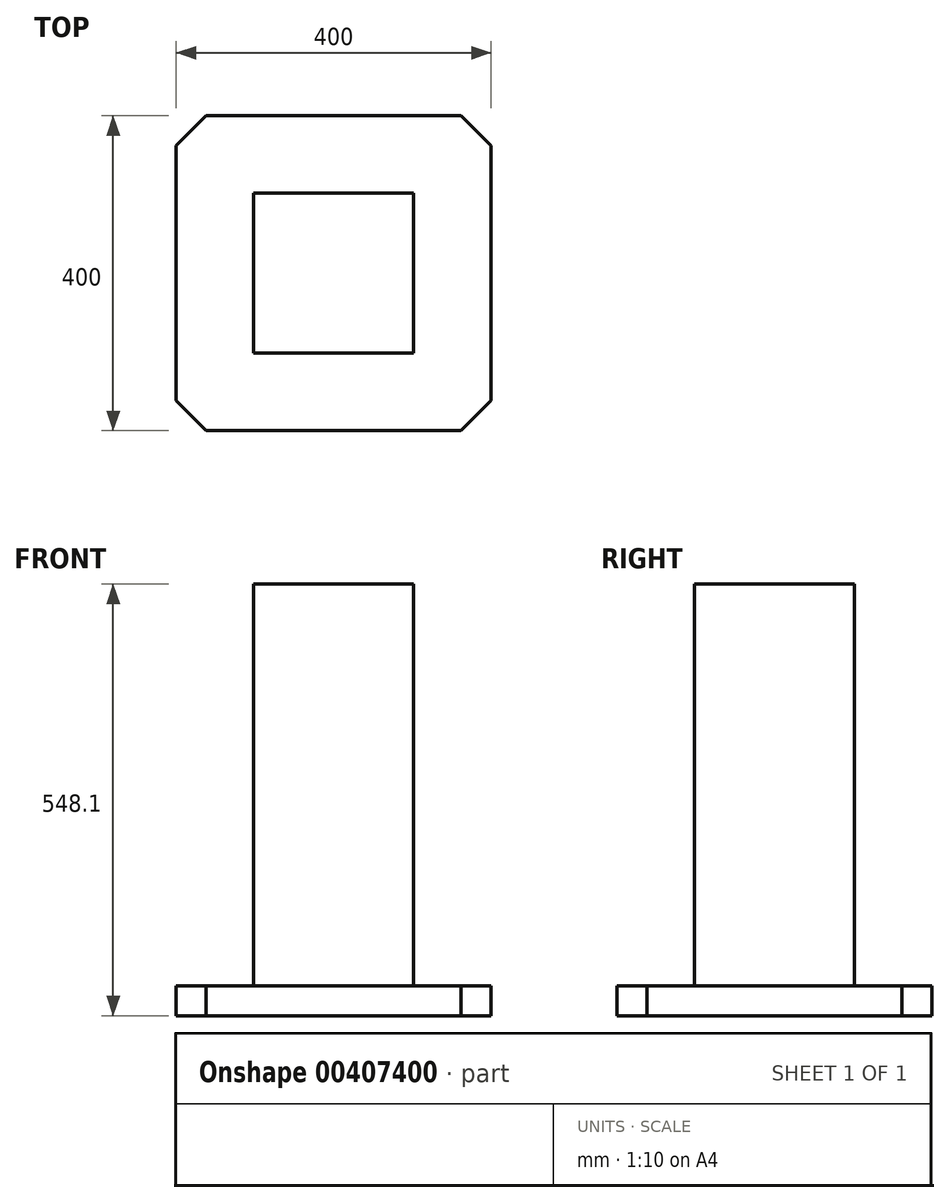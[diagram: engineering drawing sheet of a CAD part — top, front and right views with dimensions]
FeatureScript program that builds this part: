
annotation { "Feature Type Name" : "Feature", "Feature Type Description" : "" }
export const myFeature = defineFeature(function(context is Context, id is Id, definition is map)
    precondition{}
    {
        {
            var Q0;
            Q0=qCreatedBy(makeId("Top.planeOp"),FACE);
            var sketch = newSketch(context, id + "F0", { "sketchPlane" : qUnion([Q0])});
            skLineSegment(sketch, "E0.bottom", {"start": v(200, -200) * mm, "end": v(-200, -200) * mm});
            skLineSegment(sketch, "E0.top", {"start": v(200, 200) * mm, "end": v(-200, 200) * mm});
            skLineSegment(sketch, "E0.left", {"start": v(200, -200) * mm, "end": v(200, 200) * mm});
            skLineSegment(sketch, "E0.right", {"start": v(-200, -200) * mm, "end": v(-200, 200) * mm});
            skPoint(sketch, "E0.middle", {"position": v(0, 0) * mm});
            skSolve(sketch);
        }
        {
            var Q0;
            Q0=makeQuery(id+"F0.imprint","IMPRINT",FACE,{"disambiguationData":[TD([[makeQuery(id+"F0.imprint","IMPRINT",EDGE,{"derivedFrom":sQuery(id+"F0.wireOp",EDGE,"E0.bottom")}),-1.0]])]});
            extrude(context, id + "F1", {"entities" : qUnion([Q0]), "depth" : 38.1 * mm});
        }
        {
            var Q0;
            Q0=makeQuery(id+"F1.opExtrude","SWEPT_EDGE",EDGE,{"disambiguationData":[OSD([sQuery(id+"F0.wireOp",EDGE,"E0.top"),sQuery(id+"F0.wireOp",EDGE,"E0.right")])]});
            var Q1;
            Q1=makeQuery(id+"F1.opExtrude","SWEPT_EDGE",EDGE,{"disambiguationData":[OSD([sQuery(id+"F0.wireOp",EDGE,"E0.bottom"),sQuery(id+"F0.wireOp",EDGE,"E0.right")])]});
            var Q2;
            Q2=makeQuery(id+"F1.opExtrude","SWEPT_EDGE",EDGE,{"disambiguationData":[OSD([sQuery(id+"F0.wireOp",EDGE,"E0.bottom"),sQuery(id+"F0.wireOp",EDGE,"E0.left")])]});
            var Q3;
            Q3=makeQuery(id+"F1.opExtrude","SWEPT_EDGE",EDGE,{"disambiguationData":[OSD([sQuery(id+"F0.wireOp",EDGE,"E0.top"),sQuery(id+"F0.wireOp",EDGE,"E0.left")])]});
            chamfer(context, id + "F2", {"entities" : qUnion([Q0, Q1, Q2, Q3]), "width" : 38.1 * mm, "tangentPropagation" : true});
        }
        {
            var Q0;
            Q0=makeQuery(id+"F1.opExtrude","CAP_FACE",FACE,{"disambiguationData":[OSD([sQuery(id+"F0.wireOp",EDGE,"E0.bottom"),sQuery(id+"F0.wireOp",EDGE,"E0.top"),sQuery(id+"F0.wireOp",EDGE,"E0.left"),sQuery(id+"F0.wireOp",EDGE,"E0.right")])],"isStart":false});
            var sketch = newSketch(context, id + "F3", { "sketchPlane" : qUnion([Q0])});
            skLineSegment(sketch, "E1.bottom", {"start": v(101.6, -101.6) * mm, "end": v(-101.6, -101.6) * mm});
            skLineSegment(sketch, "E1.top", {"start": v(101.6, 101.6) * mm, "end": v(-101.6, 101.6) * mm});
            skLineSegment(sketch, "E1.left", {"start": v(101.6, -101.6) * mm, "end": v(101.6, 101.6) * mm});
            skLineSegment(sketch, "E1.right", {"start": v(-101.6, -101.6) * mm, "end": v(-101.6, 101.6) * mm});
            skPoint(sketch, "E1.middle", {"position": v(0, 0) * mm});
            skSolve(sketch);
        }
        {
            var Q0;
            Q0 = qSketchRegion(id + "F3", true);
            extrude(context, id + "F4", {"entities" : qUnion([Q0]), "operationType" : NewBodyOperationType.ADD, "depth" : 510 * mm});
        }
    });
